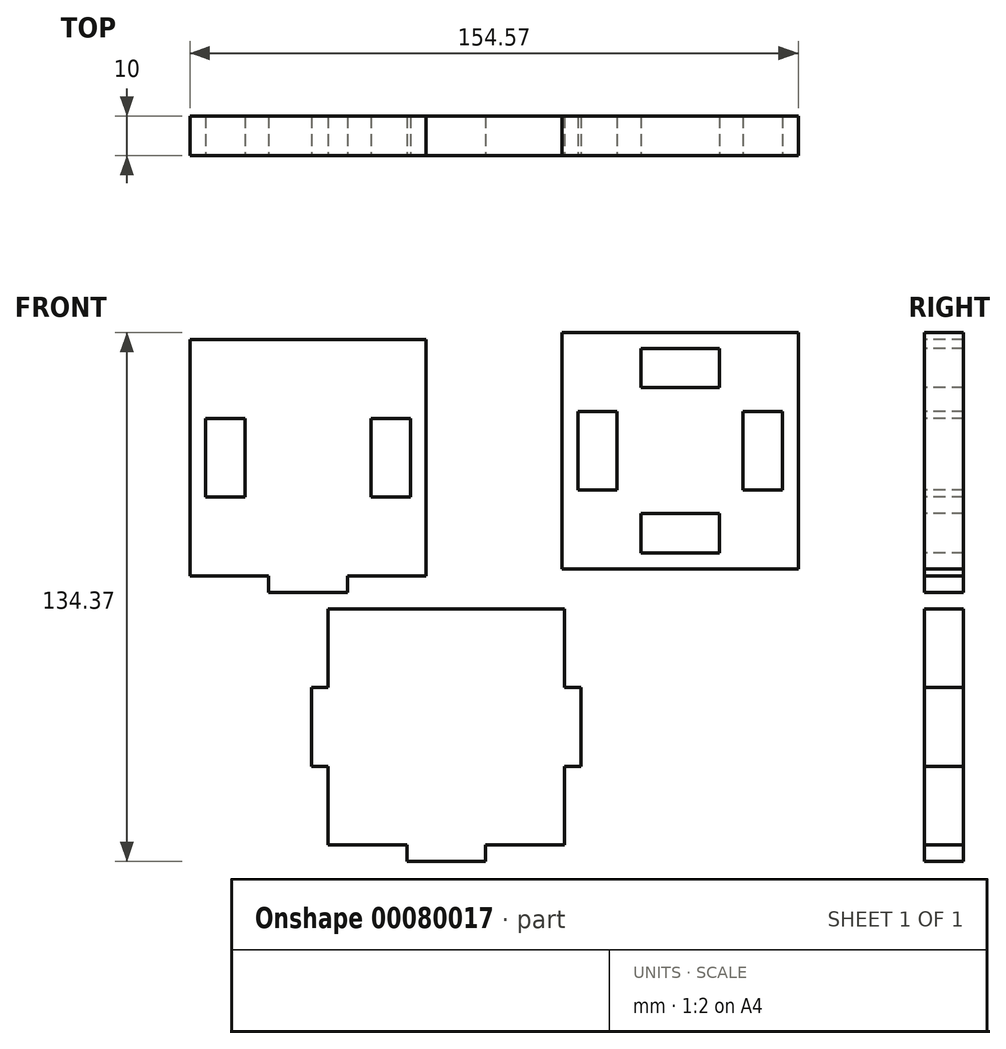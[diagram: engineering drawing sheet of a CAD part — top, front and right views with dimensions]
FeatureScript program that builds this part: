
annotation { "Feature Type Name" : "Feature", "Feature Type Description" : "" }
export const myFeature = defineFeature(function(context is Context, id is Id, definition is map)
    precondition{}
    {
        {
            var Q0;
            Q0=qCreatedBy(makeId("Front.planeOp"),FACE);
            var sketch = newSketch(context, id + "F0", { "sketchPlane" : qUnion([Q0])});
            skLineSegment(sketch, "E0.bottom", {"start": v(77.39, 57.08) * mm, "end": v(17.39, 57.08) * mm});
            skLineSegment(sketch, "E0.top", {"start": v(77.39, -2.92) * mm, "end": v(17.39, -2.92) * mm});
            skLineSegment(sketch, "E0.left", {"start": v(77.39, 57.08) * mm, "end": v(77.39, -2.92) * mm});
            skLineSegment(sketch, "E0.right", {"start": v(17.39, 57.08) * mm, "end": v(17.39, -2.92) * mm});
            skLineSegment(sketch, "E1.bottom", {"start": v(73.39, 37.08) * mm, "end": v(63.39, 37.08) * mm});
            skLineSegment(sketch, "E1.top", {"start": v(73.39, 17.08) * mm, "end": v(63.39, 17.08) * mm});
            skLineSegment(sketch, "E1.left", {"start": v(73.39, 37.08) * mm, "end": v(73.39, 17.08) * mm});
            skLineSegment(sketch, "E1.right", {"start": v(63.39, 37.08) * mm, "end": v(63.39, 17.08) * mm});
            skLineSegment(sketch, "E2.bottom", {"start": v(37.39, 53.08) * mm, "end": v(57.39, 53.08) * mm});
            skLineSegment(sketch, "E2.top", {"start": v(37.39, 43.08) * mm, "end": v(57.39, 43.08) * mm});
            skLineSegment(sketch, "E2.left", {"start": v(37.39, 53.08) * mm, "end": v(37.39, 43.08) * mm});
            skLineSegment(sketch, "E2.right", {"start": v(57.39, 53.08) * mm, "end": v(57.39, 43.08) * mm});
            skLineSegment(sketch, "E3.bottom", {"start": v(31.39, 37.08) * mm, "end": v(21.39, 37.08) * mm});
            skLineSegment(sketch, "E3.top", {"start": v(31.39, 17.08) * mm, "end": v(21.39, 17.08) * mm});
            skLineSegment(sketch, "E3.left", {"start": v(31.39, 37.08) * mm, "end": v(31.39, 17.08) * mm});
            skLineSegment(sketch, "E3.right", {"start": v(21.39, 37.08) * mm, "end": v(21.39, 17.08) * mm});
            skLineSegment(sketch, "E4.bottom", {"start": v(37.39, 11.08) * mm, "end": v(57.39, 11.08) * mm});
            skLineSegment(sketch, "E4.top", {"start": v(37.39, 1.08) * mm, "end": v(57.39, 1.08) * mm});
            skLineSegment(sketch, "E4.left", {"start": v(37.39, 11.08) * mm, "end": v(37.39, 1.08) * mm});
            skLineSegment(sketch, "E4.right", {"start": v(57.39, 11.08) * mm, "end": v(57.39, 1.08) * mm});
            skLineSegment(sketch, "E5", {"start": v(-17.18, 55.3) * mm, "end": v(-17.18, -4.7) * mm});
            skLineSegment(sketch, "E6", {"start": v(-17.18, -4.7) * mm, "end": v(-37.18, -4.7) * mm});
            skLineSegment(sketch, "E7", {"start": v(-37.18, -4.7) * mm, "end": v(-37.18, -8.9) * mm});
            skLineSegment(sketch, "E8", {"start": v(-37.18, -8.9) * mm, "end": v(-57.18, -8.9) * mm});
            skLineSegment(sketch, "E9", {"start": v(-57.18, -8.9) * mm, "end": v(-57.18, -4.7) * mm});
            skLineSegment(sketch, "E10", {"start": v(-57.18, -4.7) * mm, "end": v(-77.18, -4.7) * mm});
            skLineSegment(sketch, "E11", {"start": v(-77.18, -4.7) * mm, "end": v(-77.18, 55.3) * mm});
            skLineSegment(sketch, "E12", {"start": v(-77.18, 55.3) * mm, "end": v(-17.18, 55.3) * mm});
            skLineSegment(sketch, "E13.bottom", {"start": v(-73.18, 35.3) * mm, "end": v(-63.18, 35.3) * mm});
            skLineSegment(sketch, "E13.top", {"start": v(-73.18, 15.3) * mm, "end": v(-63.18, 15.3) * mm});
            skLineSegment(sketch, "E13.left", {"start": v(-73.18, 35.3) * mm, "end": v(-73.18, 15.3) * mm});
            skLineSegment(sketch, "E13.right", {"start": v(-63.18, 35.3) * mm, "end": v(-63.18, 15.3) * mm});
            skLineSegment(sketch, "E14.bottom", {"start": v(-31.18, 35.3) * mm, "end": v(-21.18, 35.3) * mm});
            skLineSegment(sketch, "E14.top", {"start": v(-31.18, 15.3) * mm, "end": v(-21.18, 15.3) * mm});
            skLineSegment(sketch, "E14.left", {"start": v(-31.18, 35.3) * mm, "end": v(-31.18, 15.3) * mm});
            skLineSegment(sketch, "E14.right", {"start": v(-21.18, 35.3) * mm, "end": v(-21.18, 15.3) * mm});
            skLineSegment(sketch, "E15", {"start": v(-42.06, -13.09) * mm, "end": v(-42.06, -33.09) * mm});
            skLineSegment(sketch, "E16", {"start": v(-42.06, -33.09) * mm, "end": v(-46.26, -33.09) * mm});
            skLineSegment(sketch, "E17", {"start": v(-46.26, -33.09) * mm, "end": v(-46.26, -53.09) * mm});
            skLineSegment(sketch, "E18", {"start": v(-46.26, -53.09) * mm, "end": v(-42.06, -53.09) * mm});
            skLineSegment(sketch, "E19", {"start": v(-42.06, -53.09) * mm, "end": v(-42.06, -73.09) * mm});
            skLineSegment(sketch, "E20", {"start": v(-42.06, -73.09) * mm, "end": v(-22.06, -73.09) * mm});
            skLineSegment(sketch, "E21", {"start": v(-22.06, -73.09) * mm, "end": v(-22.06, -77.29) * mm});
            skLineSegment(sketch, "E22", {"start": v(-22.06, -77.29) * mm, "end": v(-2.06, -77.29) * mm});
            skLineSegment(sketch, "E23", {"start": v(-2.06, -77.29) * mm, "end": v(-2.06, -73.09) * mm});
            skLineSegment(sketch, "E24", {"start": v(-2.06, -73.09) * mm, "end": v(17.94, -73.09) * mm});
            skLineSegment(sketch, "E25", {"start": v(17.94, -73.09) * mm, "end": v(17.94, -53.09) * mm});
            skLineSegment(sketch, "E26", {"start": v(17.94, -53.09) * mm, "end": v(22.14, -53.09) * mm});
            skLineSegment(sketch, "E27", {"start": v(22.14, -53.09) * mm, "end": v(22.14, -33.09) * mm});
            skLineSegment(sketch, "E28", {"start": v(22.14, -33.09) * mm, "end": v(17.94, -33.09) * mm});
            skLineSegment(sketch, "E29", {"start": v(17.94, -33.09) * mm, "end": v(17.94, -13.09) * mm});
            skLineSegment(sketch, "E30", {"start": v(17.94, -13.09) * mm, "end": v(-42.06, -13.09) * mm});
            skSolve(sketch);
        }
        {
            var Q0;
            Q0=sQuery(id+"F0.wireOp",EDGE,"E19");
            var Q1;
            Q1=sQuery(id+"F0.wireOp",EDGE,"E14.right");
            var Q2;
            Q2=sQuery(id+"F0.wireOp",EDGE,"E2.top");
            var Q3;
            Q3=sQuery(id+"F0.wireOp",EDGE,"E3.left");
            var Q4;
            Q4=sQuery(id+"F0.wireOp",EDGE,"E1.right");
            var Q5;
            Q5=sQuery(id+"F0.wireOp",EDGE,"E6");
            var Q6;
            Q6=sQuery(id+"F0.wireOp",EDGE,"E16");
            var Q7;
            Q7=sQuery(id+"F0.wireOp",EDGE,"E3.top");
            var Q8;
            Q8=sQuery(id+"F0.wireOp",EDGE,"E18");
            var Q9;
            Q9=sQuery(id+"F0.wireOp",EDGE,"E13.bottom");
            var Q10;
            Q10=sQuery(id+"F0.wireOp",EDGE,"E0.top");
            var Q11;
            Q11=sQuery(id+"F0.wireOp",EDGE,"E24");
            var Q12;
            Q12=sQuery(id+"F0.wireOp",EDGE,"E0.bottom");
            var Q13;
            Q13=sQuery(id+"F0.wireOp",EDGE,"E1.left");
            var Q14;
            Q14=sQuery(id+"F0.wireOp",EDGE,"E5");
            var Q15;
            Q15=sQuery(id+"F0.wireOp",EDGE,"E3.bottom");
            var Q16;
            Q16=sQuery(id+"F0.wireOp",EDGE,"E11");
            var Q17;
            Q17=sQuery(id+"F0.wireOp",EDGE,"E14.bottom");
            var Q18;
            Q18=sQuery(id+"F0.wireOp",EDGE,"E23");
            var Q19;
            Q19=sQuery(id+"F0.wireOp",EDGE,"E29");
            var Q20;
            Q20=sQuery(id+"F0.wireOp",EDGE,"E27");
            var Q21;
            Q21=sQuery(id+"F0.wireOp",EDGE,"E13.left");
            var Q22;
            Q22=sQuery(id+"F0.wireOp",EDGE,"E12");
            var Q23;
            Q23=sQuery(id+"F0.wireOp",EDGE,"E4.left");
            var Q24;
            Q24=sQuery(id+"F0.wireOp",EDGE,"E2.right");
            var Q25;
            Q25=sQuery(id+"F0.wireOp",EDGE,"E0.left");
            var Q26;
            Q26=sQuery(id+"F0.wireOp",EDGE,"E9");
            var Q27;
            Q27=sQuery(id+"F0.wireOp",EDGE,"E25");
            var Q28;
            Q28=sQuery(id+"F0.wireOp",EDGE,"E28");
            var Q29;
            Q29=sQuery(id+"F0.wireOp",EDGE,"E0.right");
            var Q30;
            Q30=sQuery(id+"F0.wireOp",EDGE,"E2.bottom");
            var Q31;
            Q31=sQuery(id+"F0.wireOp",EDGE,"E14.top");
            var Q32;
            Q32=sQuery(id+"F0.wireOp",EDGE,"E13.right");
            var Q33;
            Q33=sQuery(id+"F0.wireOp",EDGE,"E2.left");
            var Q34;
            Q34=sQuery(id+"F0.wireOp",EDGE,"E20");
            var Q35;
            Q35=sQuery(id+"F0.wireOp",EDGE,"E15");
            var Q36;
            Q36=sQuery(id+"F0.wireOp",EDGE,"E7");
            var Q37;
            Q37=sQuery(id+"F0.wireOp",EDGE,"E14.left");
            var Q38;
            Q38=sQuery(id+"F0.wireOp",EDGE,"E22");
            var Q39;
            Q39=sQuery(id+"F0.wireOp",EDGE,"E3.right");
            var Q40;
            Q40=sQuery(id+"F0.wireOp",EDGE,"E4.top");
            var Q41;
            Q41=sQuery(id+"F0.wireOp",EDGE,"E8");
            var Q42;
            Q42=sQuery(id+"F0.wireOp",EDGE,"E30");
            var Q43;
            Q43=sQuery(id+"F0.wireOp",EDGE,"E21");
            var Q44;
            Q44=sQuery(id+"F0.wireOp",EDGE,"E17");
            var Q45;
            Q45=sQuery(id+"F0.wireOp",EDGE,"E13.top");
            var Q46;
            Q46=sQuery(id+"F0.wireOp",EDGE,"E4.bottom");
            var Q47;
            Q47=sQuery(id+"F0.wireOp",EDGE,"E1.top");
            var Q48;
            Q48=sQuery(id+"F0.wireOp",EDGE,"E1.bottom");
            var Q49;
            Q49=sQuery(id+"F0.wireOp",EDGE,"E4.right");
            var Q50;
            Q50=sQuery(id+"F0.wireOp",EDGE,"E10");
            var Q51;
            Q51=sQuery(id+"F0.wireOp",EDGE,"E26");
            extrude(context, id + "F1", {"bodyType" : ToolBodyType.SURFACE, "surfaceEntities" : qUnion([Q0, Q1, Q2, Q3, Q4, Q5, Q6, Q7, Q8, Q9, Q10, Q11, Q12, Q13, Q14, Q15, Q16, Q17, Q18, Q19, Q20, Q21, Q22, Q23, Q24, Q25, Q26, Q27, Q28, Q29, Q30, Q31, Q32, Q33, Q34, Q35, Q36, Q37, Q38, Q39, Q40, Q41, Q42, Q43, Q44, Q45, Q46, Q47, Q48, Q49, Q50, Q51]), "depth" : 10 * mm});
        }
    });
